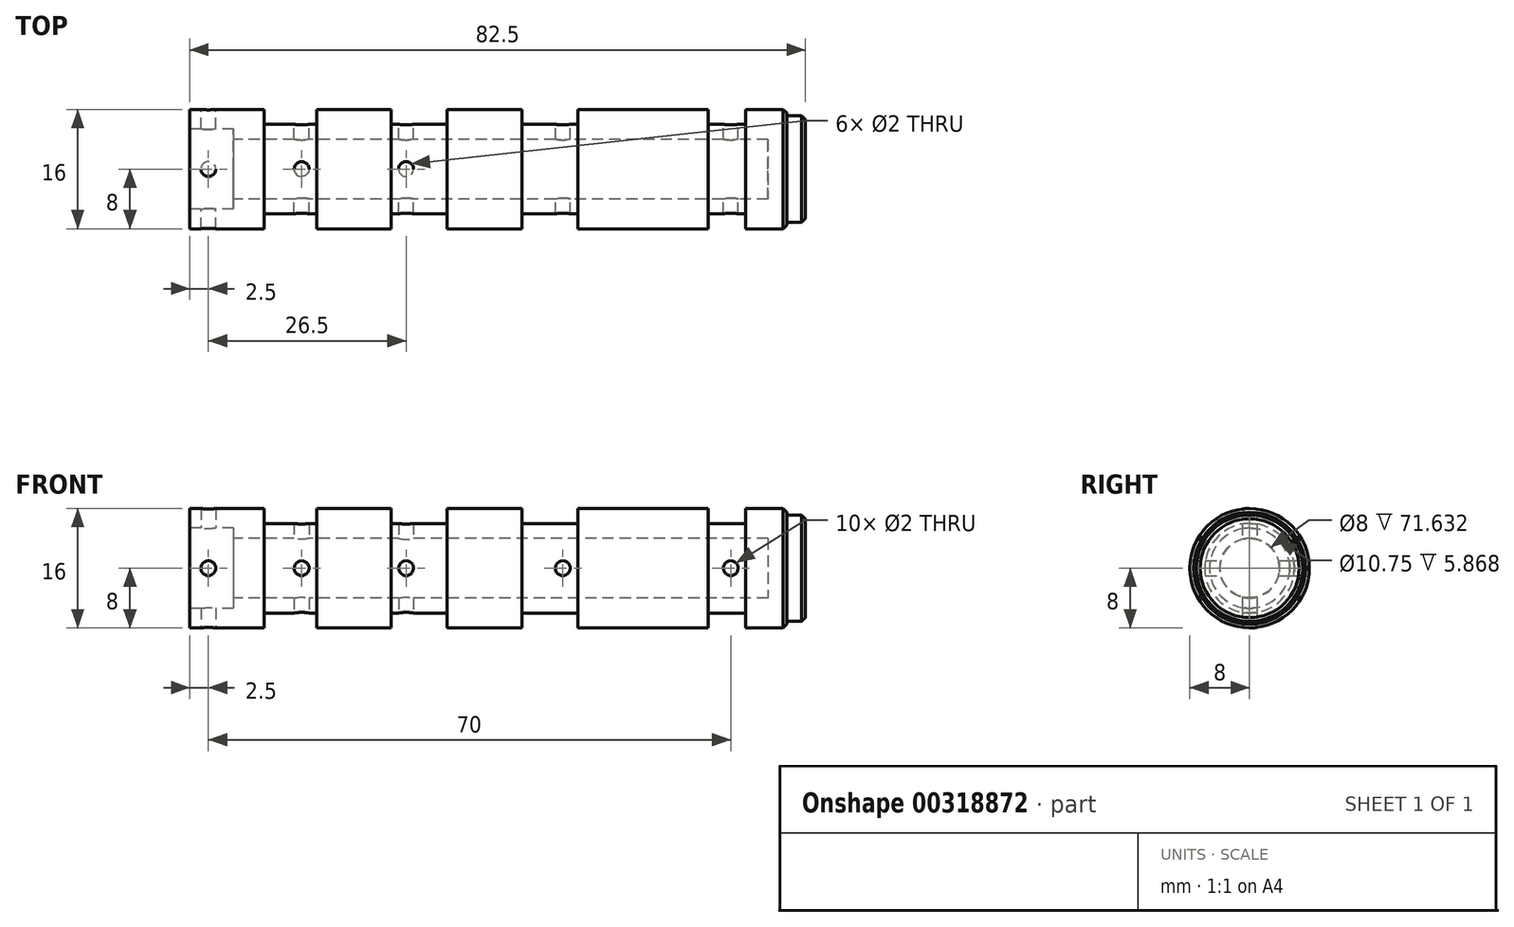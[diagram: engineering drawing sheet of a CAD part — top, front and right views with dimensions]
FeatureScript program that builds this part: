
annotation { "Feature Type Name" : "Feature", "Feature Type Description" : "" }
export const myFeature = defineFeature(function(context is Context, id is Id, definition is map)
    precondition{}
    {
        {
            var Q0;
            Q0=qCreatedBy(makeId("Front.planeOp"),FACE);
            var sketch = newSketch(context, id + "F0", { "sketchPlane" : qUnion([Q0])});
            skLineSegment(sketch, "E0", {"start": v(34.5, 8) * mm, "end": v(34.5, 6) * mm});
            skLineSegment(sketch, "E1", {"start": v(34.5, 6) * mm, "end": v(29.5, 6) * mm});
            skLineSegment(sketch, "E2", {"start": v(29.5, 6) * mm, "end": v(29.5, 8) * mm});
            skLineSegment(sketch, "E3", {"start": v(-23, 8) * mm, "end": v(-23, 6) * mm});
            skLineSegment(sketch, "E4", {"start": v(-23, 6) * mm, "end": v(-30, 6) * mm});
            skLineSegment(sketch, "E5", {"start": v(-30, 6) * mm, "end": v(-30, 8) * mm});
            skLineSegment(sketch, "E6", {"start": v(-5.5, 8) * mm, "end": v(-5.5, 6) * mm});
            skLineSegment(sketch, "E7", {"start": v(-5.5, 6) * mm, "end": v(-13, 6) * mm});
            skLineSegment(sketch, "E8", {"start": v(-13, 6) * mm, "end": v(-13, 8) * mm});
            skLineSegment(sketch, "E9", {"start": v(12, 8) * mm, "end": v(12, 6) * mm});
            skLineSegment(sketch, "E10", {"start": v(12, 6) * mm, "end": v(4.5, 6) * mm});
            skLineSegment(sketch, "E11", {"start": v(4.5, 6) * mm, "end": v(4.5, 8) * mm});
            skLineSegment(sketch, "E12", {"start": v(-40, 8) * mm, "end": v(-30, 8) * mm});
            skLineSegment(sketch, "E13", {"start": v(-23, 8) * mm, "end": v(-13, 8) * mm});
            skLineSegment(sketch, "E14", {"start": v(-5.5, 8) * mm, "end": v(4.5, 8) * mm});
            skLineSegment(sketch, "E15", {"start": v(12, 8) * mm, "end": v(29.5, 8) * mm});
            skLineSegment(sketch, "E16", {"start": v(34.5, 8) * mm, "end": v(40, 8) * mm});
            skLineSegment(sketch, "E17", {"start": v(40, 8) * mm, "end": v(40, 4) * mm});
            skLineSegment(sketch, "E18", {"start": v(-46.58, 0) * mm, "end": v(50.32, 0) * mm, "construction": true});
            skLineSegment(sketch, "E19", {"start": v(-40, 5.38) * mm, "end": v(-34.13, 5.38) * mm});
            skLineSegment(sketch, "E20", {"start": v(-34.13, 5.38) * mm, "end": v(-34.13, 4) * mm});
            skLineSegment(sketch, "E21", {"start": v(-34.13, 4) * mm, "end": v(40, 4) * mm});
            skLineSegment(sketch, "E22", {"start": v(-40, 8) * mm, "end": v(-40, 5.38) * mm});
            skSolve(sketch);
        }
        {
            var Q0;
            Q0=makeQuery(id+"F0.imprint","IMPRINT",FACE,{"disambiguationData":[TD([[makeQuery(id+"F0.imprint","IMPRINT",EDGE,{"derivedFrom":sQuery(id+"F0.wireOp",EDGE,"E0")}),1.0]])]});
            var Q1;
            Q1=sQuery(id+"F0.wireOp",EDGE,"E18");
            revolve(context, id + "F1", {"entities" : qUnion([Q0]), "axis" : qUnion([Q1]), "revolveType" : RevolveType.FULL});
        }
        {
            var Q0;
            Q0=qCreatedBy(makeId("Front.planeOp"),FACE);
            var sketch = newSketch(context, id + "F2", { "sketchPlane" : qUnion([Q0])});
            skCircle(sketch, "E23", {"center": v(-37.5, 0) * mm, "radius": 1 * mm});
            skCircle(sketch, "E24", {"center": v(-25, 0) * mm, "radius": 1 * mm});
            skCircle(sketch, "E25", {"center": v(-11, 0) * mm, "radius": 1 * mm});
            skCircle(sketch, "E26", {"center": v(10, 0) * mm, "radius": 1 * mm});
            skCircle(sketch, "E27", {"center": v(32.5, 0) * mm, "radius": 1 * mm});
            skSolve(sketch);
        }
        {
            var Q0;
            Q0 = qSketchRegion(id + "F2", true);
            extrude(context, id + "F3", {"entities" : qUnion([Q0]), "operationType" : NewBodyOperationType.REMOVE, "depth" : 25 * mm, "hasSecondDirection" : true, "secondDirectionOppositeDirection" : true, "secondDirectionDepth" : 25 * mm});
        }
        {
            var Q0;
            Q0=qCreatedBy(makeId("Top.planeOp"),FACE);
            var sketch = newSketch(context, id + "F4", { "sketchPlane" : qUnion([Q0])});
            skCircle(sketch, "E28", {"center": v(-37.5, 0) * mm, "radius": 1 * mm});
            skCircle(sketch, "E29", {"center": v(-25, 0) * mm, "radius": 1 * mm});
            skCircle(sketch, "E30", {"center": v(-11, 0) * mm, "radius": 1 * mm});
            skSolve(sketch);
        }
        {
            var Q0;
            Q0 = qSketchRegion(id + "F4", true);
            extrude(context, id + "F5", {"entities" : qUnion([Q0]), "operationType" : NewBodyOperationType.REMOVE, "depth" : 25 * mm, "hasSecondDirection" : true, "secondDirectionOppositeDirection" : true, "secondDirectionDepth" : 25 * mm});
        }
        {
            var Q0;
            Q0=makeQuery(id+"F1.opRevolve","SWEPT_EDGE",EDGE,{"disambiguationData":[OSD([sQuery(id+"F0.wireOp",EDGE,"E16"),sQuery(id+"F0.wireOp",EDGE,"E17")])]});
            chamfer(context, id + "F6", {"entities" : qUnion([Q0]), "width" : 0.5 * mm, "tangentPropagation" : true});
        }
        {
            var Q0;
            Q0=makeQuery(id+"F1.opRevolve","SWEPT_FACE",FACE,{"disambiguationData":[OSD([sQuery(id+"F0.wireOp",EDGE,"E17")])]});
            var sketch = newSketch(context, id + "F7", { "sketchPlane" : qUnion([Q0])});
            skCircle(sketch, "E31", {"center": v(0, 0) * mm, "radius": 7.12 * mm});
            skSolve(sketch);
        }
        {
            var Q0;
            Q0 = qSketchRegion(id + "F7", true);
            extrude(context, id + "F8", {"entities" : qUnion([Q0]), "depth" : 2.5 * mm});
        }
        {
            var Q0;
            Q0=makeQuery(id+"F8.opExtrude","CAP_EDGE",EDGE,{"disambiguationData":[OSD([sQuery(id+"F7.wireOp",EDGE,"E31")])],"isStart":false});
            chamfer(context, id + "F9", {"entities" : qUnion([Q0]), "width" : 0.5 * mm, "tangentPropagation" : true});
        }
        {
            var Q0;
            Q0=makeQuery(id+"F8.opExtrude","CAP_FACE",FACE,{"disambiguationData":[OSD([sQuery(id+"F7.wireOp",EDGE,"E31")])],"isStart":true});
            var sketch = newSketch(context, id + "F10", { "sketchPlane" : qUnion([Q0])});
            skCircle(sketch, "E32", {"center": v(0, 0) * mm, "radius": 4 * mm});
            skSolve(sketch);
        }
        {
            var Q0;
            Q0=makeQuery(id+"F10.imprint","IMPRINT",FACE,{"disambiguationData":[TD([[makeQuery(id+"F10.imprint","IMPRINT",EDGE,{"derivedFrom":sQuery(id+"F10.wireOp",EDGE,"E32")}),1.0]])]});
            extrude(context, id + "F11", {"entities" : qUnion([Q0]), "operationType" : NewBodyOperationType.ADD, "depth" : 2.5 * mm});
        }
    });
